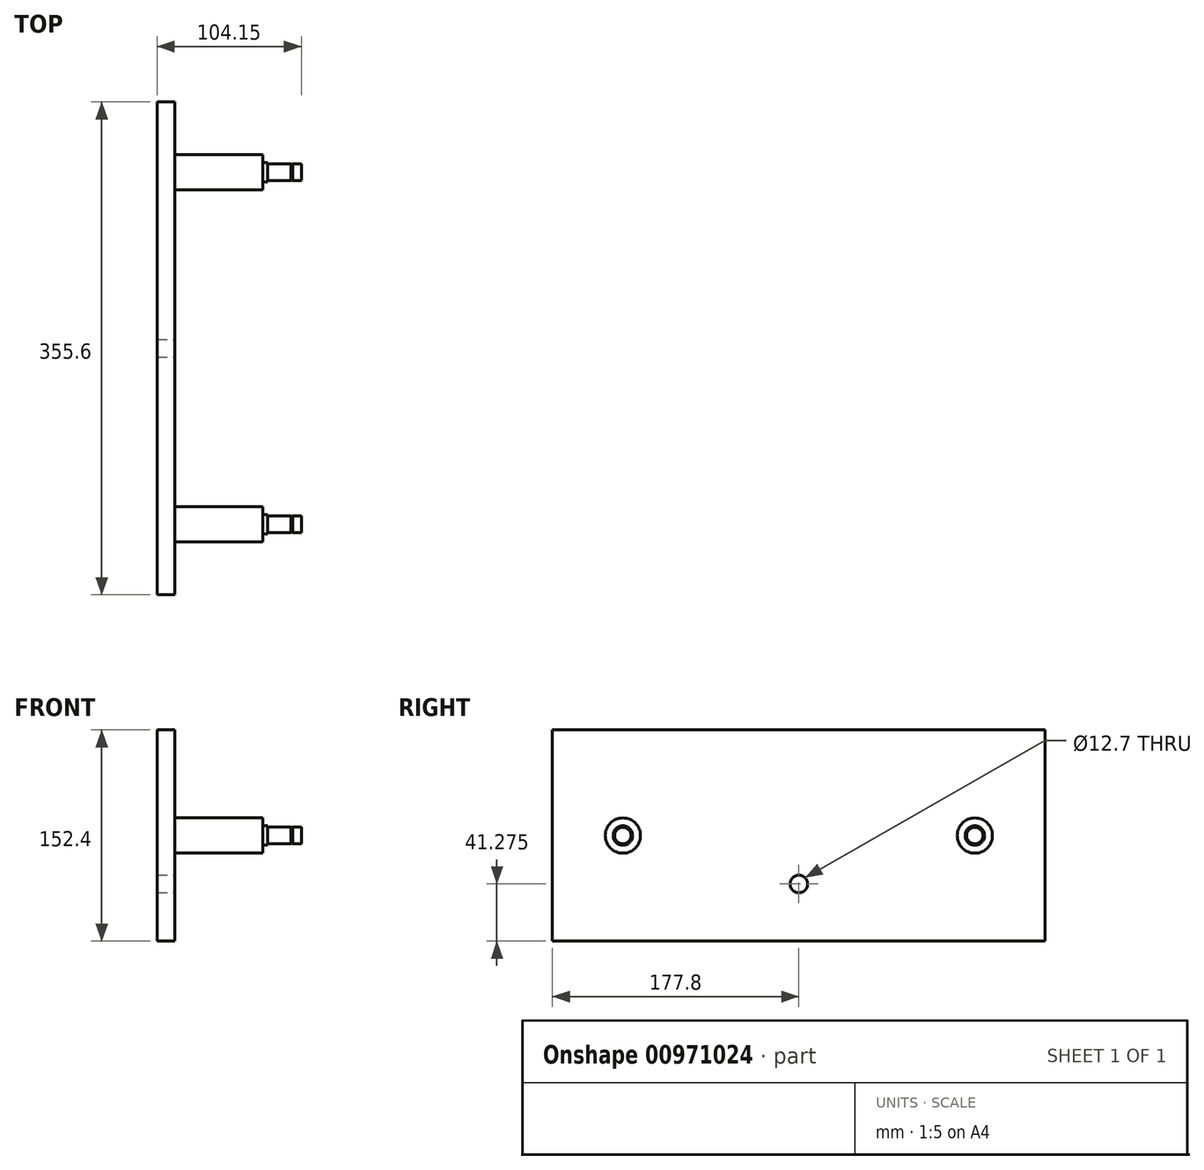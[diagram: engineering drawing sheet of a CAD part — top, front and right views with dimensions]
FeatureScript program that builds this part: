
annotation { "Feature Type Name" : "Feature", "Feature Type Description" : "" }
export const myFeature = defineFeature(function(context is Context, id is Id, definition is map)
    precondition{}
    {
        {
            var Q0;
            Q0=qCreatedBy(makeId("Right.planeOp"),FACE);
            var sketch = newSketch(context, id + "F0", { "sketchPlane" : qUnion([Q0])});
            skLineSegment(sketch, "E0.bottom", {"start": v(0, 0) * mm, "end": v(355.6, 0) * mm});
            skLineSegment(sketch, "E0.top", {"start": v(0, 152.4) * mm, "end": v(355.6, 152.4) * mm});
            skLineSegment(sketch, "E0.left", {"start": v(0, 0) * mm, "end": v(0, 152.4) * mm});
            skLineSegment(sketch, "E0.right", {"start": v(355.6, 0) * mm, "end": v(355.6, 152.4) * mm});
            skSolve(sketch);
        }
        {
            var Q0;
            Q0 = qSketchRegion(id + "F0", true);
            extrude(context, id + "F1", {"entities" : qUnion([Q0]), "depth" : 12.7 * mm, "offsetDistance" : 25.4 * mm});
        }
        {
            var Q0;
            Q0=makeQuery(id+"F1.opExtrude","CAP_FACE",FACE,{"disambiguationData":[OSD([sQuery(id+"F0.wireOp",EDGE,"E0.bottom"),sQuery(id+"F0.wireOp",EDGE,"E0.top"),sQuery(id+"F0.wireOp",EDGE,"E0.left"),sQuery(id+"F0.wireOp",EDGE,"E0.right")])],"isStart":false});
            var sketch = newSketch(context, id + "F2", { "sketchPlane" : qUnion([Q0])});
            skLineSegment(sketch, "E1", {"start": v(0, 76.2) * mm, "end": v(355.6, 76.2) * mm});
            skCircle(sketch, "E2", {"center": v(50.8, 76.2) * mm, "radius": 12.7 * mm});
            skCircle(sketch, "E3", {"center": v(304.8, 76.2) * mm, "radius": 12.7 * mm});
            skSolve(sketch);
        }
        {
            var Q0;
            Q0 = qSketchRegion(id + "F2", true);
            extrude(context, id + "F3", {"entities" : qUnion([Q0]), "operationType" : NewBodyOperationType.ADD, "depth" : 63.5 * mm, "offsetDistance" : 25.4 * mm});
        }
        {
            var Q0;
            Q0=makeQuery(id+"F3.opExtrude","CAP_FACE",FACE,{"disambiguationData":[OSD([sQuery(id+"F2.wireOp",EDGE,"E2")])],"isStart":false});
            var sketch = newSketch(context, id + "F4", { "sketchPlane" : qUnion([Q0])});
            skCircle(sketch, "E4", {"center": v(50.8, 76.2) * mm, "radius": 7 * mm});
            skSolve(sketch);
        }
        {
            var Q0;
            Q0 = qSketchRegion(id + "F4", true);
            extrude(context, id + "F5", {"entities" : qUnion([Q0]), "operationType" : NewBodyOperationType.ADD, "depth" : 3.5 * mm, "offsetDistance" : 25.4 * mm});
        }
        {
            var Q0;
            Q0=makeQuery(id+"F3.opExtrude","CAP_FACE",FACE,{"disambiguationData":[OSD([sQuery(id+"F2.wireOp",EDGE,"E3")])],"isStart":false});
            var sketch = newSketch(context, id + "F6", { "sketchPlane" : qUnion([Q0])});
            skCircle(sketch, "E5", {"center": v(304.8, 76.2) * mm, "radius": 7 * mm});
            skSolve(sketch);
        }
        {
            var Q0;
            Q0 = qSketchRegion(id + "F6", true);
            extrude(context, id + "F7", {"entities" : qUnion([Q0]), "operationType" : NewBodyOperationType.ADD, "depth" : 3.5 * mm, "offsetDistance" : 25.4 * mm});
        }
        {
            var Q0;
            Q0=makeQuery(id+"F5.opExtrude","CAP_FACE",FACE,{"disambiguationData":[OSD([sQuery(id+"F4.wireOp",EDGE,"E4")])],"isStart":false});
            var sketch = newSketch(context, id + "F8", { "sketchPlane" : qUnion([Q0])});
            skCircle(sketch, "E6", {"center": v(50.8, 76.2) * mm, "radius": 6 * mm});
            skSolve(sketch);
        }
        {
            var Q0;
            Q0 = qSketchRegion(id + "F8", true);
            extrude(context, id + "F9", {"entities" : qUnion([Q0]), "operationType" : NewBodyOperationType.ADD, "depth" : 17 * mm, "offsetDistance" : 25.4 * mm});
        }
        {
            var Q0;
            Q0=makeQuery(id+"F7.opExtrude","CAP_FACE",FACE,{"disambiguationData":[OSD([sQuery(id+"F6.wireOp",EDGE,"E5")])],"isStart":false});
            var sketch = newSketch(context, id + "F10", { "sketchPlane" : qUnion([Q0])});
            skCircle(sketch, "E7", {"center": v(304.8, 76.2) * mm, "radius": 6 * mm});
            skSolve(sketch);
        }
        {
            var Q0;
            Q0 = qSketchRegion(id + "F10", true);
            extrude(context, id + "F11", {"entities" : qUnion([Q0]), "operationType" : NewBodyOperationType.ADD, "depth" : 17 * mm, "offsetDistance" : 25.4 * mm});
        }
        {
            var Q0;
            Q0=makeQuery(id+"F9.opExtrude","CAP_FACE",FACE,{"disambiguationData":[OSD([sQuery(id+"F8.wireOp",EDGE,"E6")])],"isStart":false});
            var sketch = newSketch(context, id + "F12", { "sketchPlane" : qUnion([Q0])});
            skCircle(sketch, "E8", {"center": v(50.8, 76.2) * mm, "radius": 5.75 * mm});
            skSolve(sketch);
        }
        {
            var Q0;
            Q0 = qSketchRegion(id + "F12", true);
            extrude(context, id + "F13", {"entities" : qUnion([Q0]), "operationType" : NewBodyOperationType.ADD, "depth" : 1.1 * mm, "offsetDistance" : 25.4 * mm});
        }
        {
            var Q0;
            Q0=makeQuery(id+"F11.opExtrude","CAP_FACE",FACE,{"disambiguationData":[OSD([sQuery(id+"F10.wireOp",EDGE,"E7")])],"isStart":false});
            var sketch = newSketch(context, id + "F14", { "sketchPlane" : qUnion([Q0])});
            skCircle(sketch, "E9", {"center": v(304.8, 76.2) * mm, "radius": 5.75 * mm});
            skSolve(sketch);
        }
        {
            var Q0;
            Q0 = qSketchRegion(id + "F14", true);
            extrude(context, id + "F15", {"entities" : qUnion([Q0]), "operationType" : NewBodyOperationType.ADD, "depth" : 1.1 * mm, "offsetDistance" : 25.4 * mm});
        }
        {
            var Q0;
            Q0=makeQuery(id+"F13.opExtrude","CAP_FACE",FACE,{"disambiguationData":[OSD([sQuery(id+"F12.wireOp",EDGE,"E8")])],"isStart":false});
            var sketch = newSketch(context, id + "F16", { "sketchPlane" : qUnion([Q0])});
            skCircle(sketch, "E10", {"center": v(50.8, 76.2) * mm, "radius": 6 * mm});
            skSolve(sketch);
        }
        {
            var Q0;
            Q0 = qSketchRegion(id + "F16", true);
            extrude(context, id + "F17", {"entities" : qUnion([Q0]), "operationType" : NewBodyOperationType.ADD, "depth" : 6.35 * mm, "offsetDistance" : 25.4 * mm});
        }
        {
            var Q0;
            Q0=makeQuery(id+"F15.opExtrude","CAP_FACE",FACE,{"disambiguationData":[OSD([sQuery(id+"F14.wireOp",EDGE,"E9")])],"isStart":false});
            var sketch = newSketch(context, id + "F18", { "sketchPlane" : qUnion([Q0])});
            skCircle(sketch, "E11", {"center": v(304.8, 76.2) * mm, "radius": 6 * mm});
            skSolve(sketch);
        }
        {
            var Q0;
            Q0 = qSketchRegion(id + "F18", true);
            extrude(context, id + "F19", {"entities" : qUnion([Q0]), "operationType" : NewBodyOperationType.ADD, "depth" : 6.35 * mm, "offsetDistance" : 25.4 * mm});
        }
        {
            var Q0;
            Q0=makeQuery(id+"F1.opExtrude","CAP_FACE",FACE,{"disambiguationData":[OSD([sQuery(id+"F0.wireOp",EDGE,"E0.bottom"),sQuery(id+"F0.wireOp",EDGE,"E0.top"),sQuery(id+"F0.wireOp",EDGE,"E0.left"),sQuery(id+"F0.wireOp",EDGE,"E0.right")])],"isStart":false});
            var sketch = newSketch(context, id + "F20", { "sketchPlane" : qUnion([Q0])});
            skCircle(sketch, "E12", {"center": v(177.8, 41.28) * mm, "radius": 6.35 * mm});
            skSolve(sketch);
        }
        {
            var Q0;
            Q0 = qSketchRegion(id + "F20", true);
            extrude(context, id + "F21", {"entities" : qUnion([Q0]), "operationType" : NewBodyOperationType.REMOVE, "oppositeDirection" : true, "depth" : 25.4 * mm, "offsetDistance" : 25.4 * mm});
        }
    });
